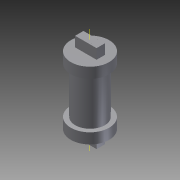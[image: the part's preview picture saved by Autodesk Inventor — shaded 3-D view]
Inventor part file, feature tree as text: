
AUTODESK INVENTOR PART (.ipt)
format: ipt  version: 2012 (Build 160160000, 160)  size: 224,256 bytes
history: native  units: mm
features: extrude x17, sketch x17, projected_geometry x5, other x1, reference x1
ambient origin geometry x8: Origin, YZ Plane, XZ Plane, XY Plane, X Axis, Y Axis, Z Axis, Center Point
bodies: Solid1 (feature_tree)
feature tree (41):
  extrude  "Extrusion1"  Depth=2.0mm TaperAngle=0.0deg
  extrude  "Extrusion2"  Depth=2.0mm TaperAngle=0.0deg
  extrude  "Extrusion3"  Depth=4.909mm
  extrude  "Extrusion4"  Depth=1.909188mm
  extrude  "Extrusion5"  Depth=2.0mm
  extrude  "Extrusion6"  Depth=10.0mm TaperAngle=0.0deg
  extrude  "Extrusion7"  Depth=2.7mm
  extrude  "Extrusion8"  Depth=10.0mm TaperAngle=0.0deg
  extrude  "Extrusion9"  Depth=10.0mm TaperAngle=0.0deg
  extrude  "Extrusion11"  Depth=0.3mm TaperAngle=0.0deg
  extrude  "Extrusion12"  Depth=8.2mm
  other  "Work Axis1"
  extrude  "Extrusion13"  Depth=8.75mm
  extrude  "Extrusion14"  Depth=8.75mm
  extrude  "Extrusion15"  Depth=10.0mm TaperAngle=0.0deg
  extrude  "Extrusion16"  Depth=10.0mm TaperAngle=0.0deg
  extrude  "Extrusion17"  Depth=10.0mm TaperAngle=0.0deg
  extrude  "Extrusion18"  [1 undecoded]
  sketch  "Sketch1"  dims[d1=5.0mm d2=15.0mm d3=0.0mm d4=0.0mm d5=2.0mm d6=0.0mm]
  reference  "Reference1"
  sketch  "Sketch2"  dims[d7=2.7mm d8=0.0mm d9=2.0mm d10=0.0mm]
  projected_geometry  "Projected Loop1"
  sketch  "Sketch3"  dims[d11=2.7mm d12=0.0mm d13=4.909mm]
  projected_geometry  "Projected Loop2"
  sketch  "Sketch4"  dims[d14=1.499906mm d15=1.909188mm]
  projected_geometry  "Projected Loop3"
  projected_geometry  "Projected Loop4"
  sketch  "Sketch5"  dims[d16=2.0mm d17=2.0mm]
  sketch  "Sketch7"  dims[d18=0.0mm d19=10.0mm d20=0.0mm]
  sketch  "Sketch8"  dims[d21=2.7mm d22=2.7mm]
  sketch  "Sketch9"  dims[d23=6.75mm d24=10.0mm d25=0.0mm]
  sketch  "Sketch10"  dims[d26=1.0mm d27=10.0mm d28=0.0mm]
  sketch  "Sketch12"  dims[d29=10.0mm d30=0.0mm d33=0.3mm d34=0.0mm]
  sketch  "Sketch13"  dims[d35=0.3mm d36=0.0mm d37=8.2mm]
  sketch  "Sketch14"  dims[d38=10.0mm d39=0.0mm d40=8.75mm]
  sketch  "Sketch15"  dims[d41=8.75mm d42=8.75mm]
  sketch  "Sketch16"  dims[d43=10.0mm d44=0.0mm d45=10.0mm d46=0.0mm]
  projected_geometry  "Projected Loop5"
  sketch  "Sketch17"  dims[d47=10.0mm d48=0.0mm d49=10.0mm d50=0.0mm]
  sketch  "Sketch18"  dims[d51=1.5mm d52=10.0mm d53=0.0mm]
  sketch  "Sketch19"
note: 1 required parameter value undecoded (feature->parameter linkage not recoverable at this tier; creation-order binding heuristic only, values carry confidence <= 0.55)
